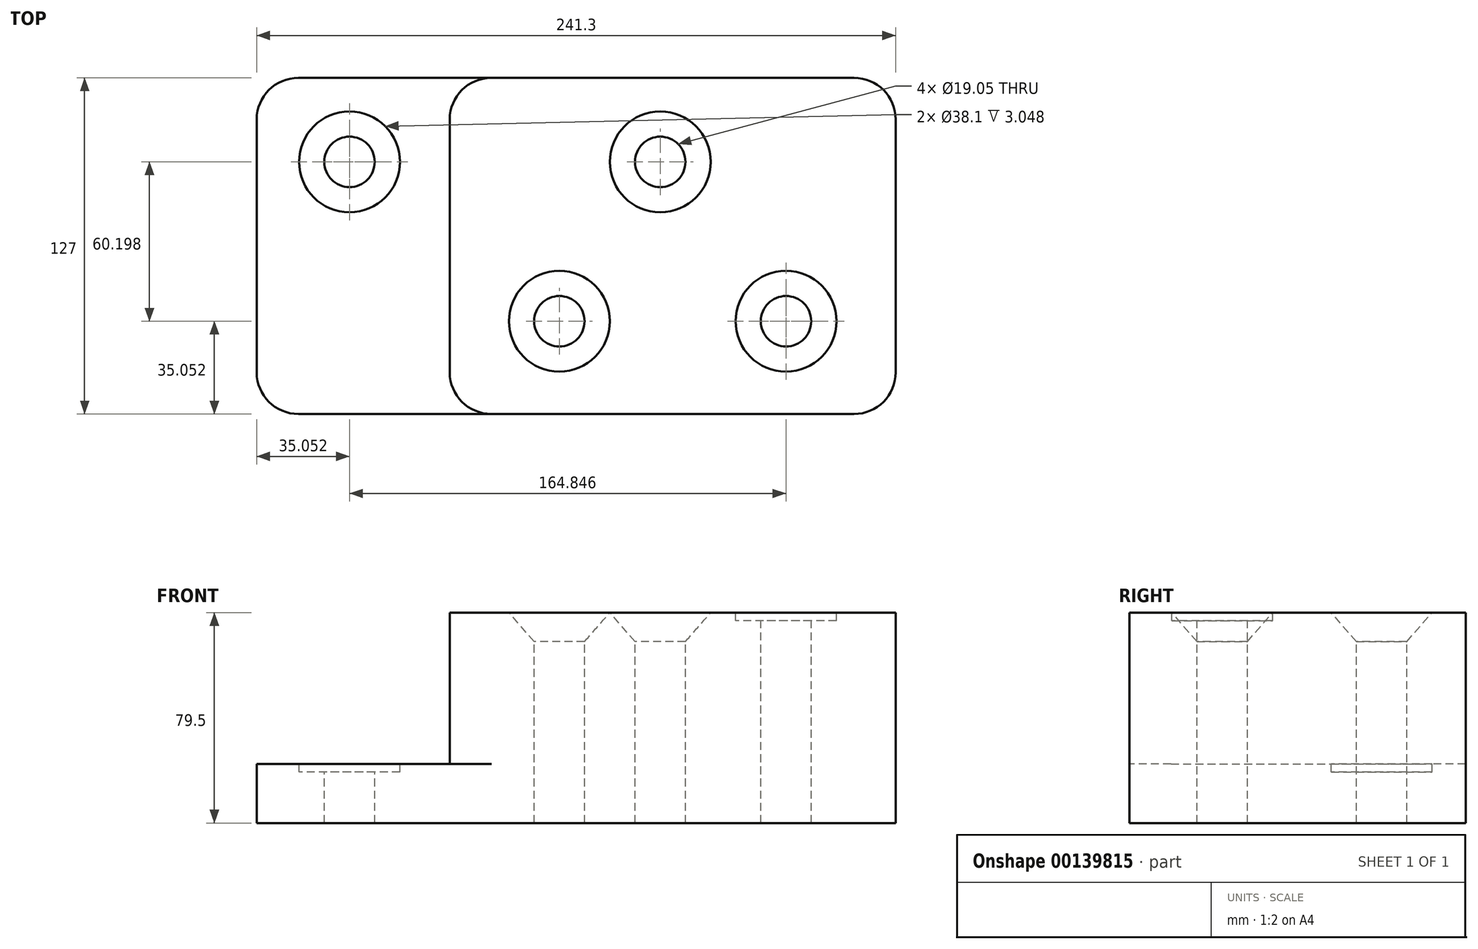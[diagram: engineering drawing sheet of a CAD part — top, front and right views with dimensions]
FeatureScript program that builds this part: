
annotation { "Feature Type Name" : "Feature", "Feature Type Description" : "" }
export const myFeature = defineFeature(function(context is Context, id is Id, definition is map)
    precondition{}
    {
        {
            var Q0;
            Q0=qCreatedBy(makeId("Top.planeOp"),FACE);
            var sketch = newSketch(context, id + "F0", { "sketchPlane" : qUnion([Q0])});
            skLineSegment(sketch, "E0.bottom", {"start": v(104.9, -63.5) * mm, "end": v(-104.9, -63.5) * mm});
            skLineSegment(sketch, "E0.top", {"start": v(104.9, 63.5) * mm, "end": v(-104.9, 63.5) * mm});
            skLineSegment(sketch, "E0.left", {"start": v(120.65, -47.75) * mm, "end": v(120.65, 47.75) * mm});
            skLineSegment(sketch, "E0.right", {"start": v(-120.65, -47.75) * mm, "end": v(-120.65, 47.75) * mm});
            skPoint(sketch, "E0.middle", {"position": v(0, 0) * mm});
            skPoint(sketch, "E1.visualSharp", {"position": v(-120.65, 63.5) * mm});
            skArc(sketch, "E1.filletArc", {"start": v(-104.9, 63.5) * mm, "mid": v(-116.04, 58.89) * mm, "end": v(-120.65, 47.75) * mm});
            skPoint(sketch, "E2.visualSharp", {"position": v(120.65, 63.5) * mm});
            skArc(sketch, "E2.filletArc", {"start": v(120.65, 47.75) * mm, "mid": v(116.04, 58.89) * mm, "end": v(104.9, 63.5) * mm});
            skPoint(sketch, "E3.visualSharp", {"position": v(-120.65, -63.5) * mm});
            skArc(sketch, "E3.filletArc", {"start": v(-120.65, -47.75) * mm, "mid": v(-116.04, -58.89) * mm, "end": v(-104.9, -63.5) * mm});
            skPoint(sketch, "E4.visualSharp", {"position": v(120.65, -63.5) * mm});
            skArc(sketch, "E4.filletArc", {"start": v(104.9, -63.5) * mm, "mid": v(116.04, -58.89) * mm, "end": v(120.65, -47.75) * mm});
            skCircle(sketch, "E5", {"center": v(-85.6, 31.75) * mm, "radius": 7.24 * mm});
            skSolve(sketch);
        }
        {
            var Q0;
            Q0=makeQuery(id+"F0.imprint","IMPRINT",FACE,{"disambiguationData":[TD([[makeQuery(id+"F0.imprint","IMPRINT",EDGE,{"derivedFrom":sQuery(id+"F0.wireOp",EDGE,"E0.bottom")}),-1.0]])]});
            var Q1;
            Q1=makeQuery(id+"F0.imprint","IMPRINT",FACE,{"disambiguationData":[TD([[makeQuery(id+"F0.imprint","IMPRINT",EDGE,{"derivedFrom":sQuery(id+"F0.wireOp",EDGE,"E5")}),1.0]])]});
            extrude(context, id + "F1", {"entities" : qUnion([Q0, Q1]), "oppositeDirection" : true, "depth" : 22.35 * mm});
        }
        {
            var Q0;
            Q0=makeQuery(id+"F1.opExtrude","CAP_FACE",FACE,{"disambiguationData":[OSD([sQuery(id+"F0.wireOp",EDGE,"E0.bottom"),sQuery(id+"F0.wireOp",EDGE,"E0.top"),sQuery(id+"F0.wireOp",EDGE,"E0.left"),sQuery(id+"F0.wireOp",EDGE,"E0.right"),sQuery(id+"F0.wireOp",EDGE,"E1.filletArc"),sQuery(id+"F0.wireOp",EDGE,"E2.filletArc"),sQuery(id+"F0.wireOp",EDGE,"E3.filletArc"),sQuery(id+"F0.wireOp",EDGE,"E4.filletArc")])],"isStart":true});
            var sketch = newSketch(context, id + "F2", { "sketchPlane" : qUnion([Q0])});
            skLineSegment(sketch, "E6", {"start": v(-47.75, 47.75) * mm, "end": v(-47.75, -47.75) * mm});
            skLineSegment(sketch, "E7", {"start": v(120.65, 47.75) * mm, "end": v(120.65, -47.75) * mm});
            skLineSegment(sketch, "E8", {"start": v(104.9, -63.5) * mm, "end": v(-32, -63.5) * mm});
            skLineSegment(sketch, "E9", {"start": v(104.9, 63.5) * mm, "end": v(-32, 63.5) * mm});
            skPoint(sketch, "E10.visualSharp", {"position": v(120.65, 63.5) * mm});
            skArc(sketch, "E10.filletArc", {"start": v(120.65, 47.75) * mm, "mid": v(116.04, 58.89) * mm, "end": v(104.9, 63.5) * mm});
            skPoint(sketch, "E11.visualSharp", {"position": v(120.65, -63.5) * mm});
            skArc(sketch, "E11.filletArc", {"start": v(104.9, -63.5) * mm, "mid": v(116.04, -58.89) * mm, "end": v(120.65, -47.75) * mm});
            skPoint(sketch, "E12.visualSharp", {"position": v(-47.75, -63.5) * mm});
            skArc(sketch, "E12.filletArc", {"start": v(-47.75, -47.75) * mm, "mid": v(-43.14, -58.89) * mm, "end": v(-32, -63.5) * mm});
            skPoint(sketch, "E13.visualSharp", {"position": v(-47.75, 63.5) * mm});
            skArc(sketch, "E13.filletArc", {"start": v(-32, 63.5) * mm, "mid": v(-43.14, 58.89) * mm, "end": v(-47.75, 47.75) * mm});
            skSolve(sketch);
        }
        {
            var Q0;
            Q0=makeQuery(id+"F2.imprint","IMPRINT",FACE,{"disambiguationData":[TD([[makeQuery(id+"F2.imprint","IMPRINT",EDGE,{"derivedFrom":sQuery(id+"F2.wireOp",EDGE,"E6")}),1.0]])]});
            extrude(context, id + "F3", {"entities" : qUnion([Q0]), "operationType" : NewBodyOperationType.ADD, "depth" : 57.15 * mm});
        }
        {
            var Q0;
            Q0=makeQuery(id+"F3.opExtrude","CAP_FACE",FACE,{"disambiguationData":[OSD([sQuery(id+"F2.wireOp",EDGE,"E6"),sQuery(id+"F2.wireOp",EDGE,"E7"),sQuery(id+"F2.wireOp",EDGE,"E8"),sQuery(id+"F2.wireOp",EDGE,"E9"),sQuery(id+"F2.wireOp",EDGE,"E10.filletArc"),sQuery(id+"F2.wireOp",EDGE,"E11.filletArc"),sQuery(id+"F2.wireOp",EDGE,"E12.filletArc"),sQuery(id+"F2.wireOp",EDGE,"E13.filletArc")])],"isStart":false});
            var sketch = newSketch(context, id + "F4", { "sketchPlane" : qUnion([Q0])});
            skCircle(sketch, "E14", {"center": v(31.75, 31.75) * mm, "radius": 9.53 * mm});
            skCircle(sketch, "E15", {"center": v(79.25, -28.45) * mm, "radius": 9.53 * mm});
            skCircle(sketch, "E16", {"center": v(-6.35, -28.45) * mm, "radius": 9.53 * mm});
            skSolve(sketch);
        }
        {
            var Q0;
            Q0=sQuery(id+"F4.wireOp",VERTEX,"E15.center");
            var Q1;
            Q1=sQuery(id+"F0.wireOp",VERTEX,"E5.center");
            var Q2;
            Q2=makeQuery(id+"F1.opExtrude","SWEPT_BODY",BODY,{"disambiguationData":[OSD([sQuery(id+"F0.wireOp",EDGE,"E0.bottom"),sQuery(id+"F0.wireOp",EDGE,"E0.top"),sQuery(id+"F0.wireOp",EDGE,"E0.left"),sQuery(id+"F0.wireOp",EDGE,"E0.right"),sQuery(id+"F0.wireOp",EDGE,"E1.filletArc"),sQuery(id+"F0.wireOp",EDGE,"E2.filletArc"),sQuery(id+"F0.wireOp",EDGE,"E3.filletArc"),sQuery(id+"F0.wireOp",EDGE,"E4.filletArc")])]});
            hole(context, id + "F5", {"style" : HoleStyle.C_BORE, "endStyle" : HoleEndStyle.THROUGH, "holeDiameter" : 19.05 * mm, "cBoreDiameter" : 38.1 * mm, "cBoreDepth" : 3.05 * mm, "locations" : qUnion([Q0, Q1]), "scope" : qUnion([Q2]), "isTappedThrough" : true});
        }
        {
            var Q0;
            Q0=sQuery(id+"F4.wireOp",VERTEX,"E14.center");
            var Q1;
            Q1=sQuery(id+"F4.wireOp",VERTEX,"E16.center");
            var Q2;
            Q2=makeQuery(id+"F1.opExtrude","SWEPT_BODY",BODY,{"disambiguationData":[OSD([sQuery(id+"F0.wireOp",EDGE,"E0.bottom"),sQuery(id+"F0.wireOp",EDGE,"E0.top"),sQuery(id+"F0.wireOp",EDGE,"E0.left"),sQuery(id+"F0.wireOp",EDGE,"E0.right"),sQuery(id+"F0.wireOp",EDGE,"E1.filletArc"),sQuery(id+"F0.wireOp",EDGE,"E2.filletArc"),sQuery(id+"F0.wireOp",EDGE,"E3.filletArc"),sQuery(id+"F0.wireOp",EDGE,"E4.filletArc")])]});
            hole(context, id + "F6", {"style" : HoleStyle.C_SINK, "endStyle" : HoleEndStyle.THROUGH, "holeDiameter" : 19.05 * mm, "cSinkDiameter" : 38.1 * mm, "cSinkAngle" : 82 * degree, "locations" : qUnion([Q0, Q1]), "scope" : qUnion([Q2]), "isTappedThrough" : true});
        }
    });
